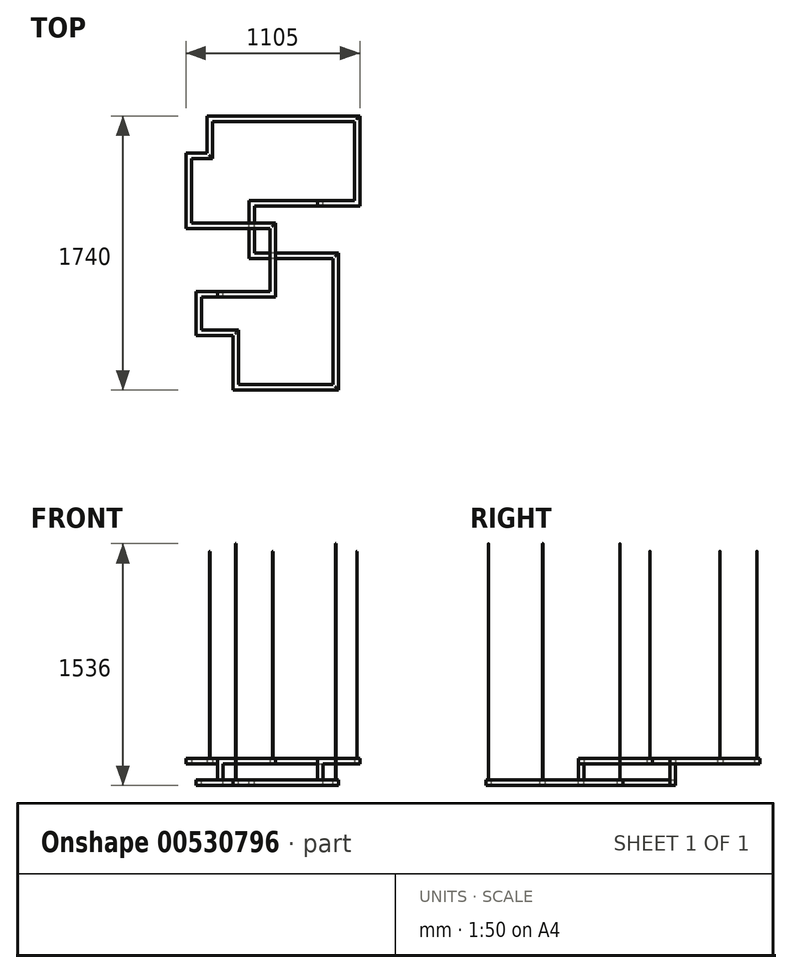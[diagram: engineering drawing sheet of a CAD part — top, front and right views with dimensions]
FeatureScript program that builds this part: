
annotation { "Feature Type Name" : "Feature", "Feature Type Description" : "" }
export const myFeature = defineFeature(function(context is Context, id is Id, definition is map)
    precondition{}
    {
        {
            var Q0;
            Q0=qCreatedBy(makeId("Top.planeOp"),FACE);
            var sketch = newSketch(context, id + "F0", { "sketchPlane" : qUnion([Q0])});
            skLineSegment(sketch, "E0", {"start": v(519.01, 860.28) * mm, "end": v(-510.57, -839.72) * mm, "construction": true});
            skLineSegment(sketch, "E1", {"start": v(-510.57, 860.28) * mm, "end": v(519.01, -839.72) * mm, "construction": true});
            skLineSegment(sketch, "E2", {"start": v(-313.44, -217.5) * mm, "end": v(-17.5, -217.5) * mm, "construction": true});
            skLineSegment(sketch, "E3", {"start": v(-17.5, -217.5) * mm, "end": v(-17.5, 217.5) * mm, "construction": true});
            skLineSegment(sketch, "E4", {"start": v(-17.5, 217.5) * mm, "end": v(-552.5, 217.5) * mm, "construction": true});
            skLineSegment(sketch, "E5", {"start": v(-552.5, 217.5) * mm, "end": v(-552.5, 662.5) * mm, "construction": true});
            skLineSegment(sketch, "E6", {"start": v(-552.5, 662.5) * mm, "end": v(-417.5, 662.5) * mm, "construction": true});
            skLineSegment(sketch, "E7", {"start": v(-417.5, 662.5) * mm, "end": v(-417.5, 897.5) * mm, "construction": true});
            skLineSegment(sketch, "E8", {"start": v(-417.5, 897.5) * mm, "end": v(517.5, 897.5) * mm, "construction": true});
            skLineSegment(sketch, "E9", {"start": v(517.5, 897.5) * mm, "end": v(517.5, 362.5) * mm, "construction": true});
            skLineSegment(sketch, "E10", {"start": v(517.5, 362.5) * mm, "end": v(294.36, 362.5) * mm, "construction": true});
            skLineSegment(sketch, "E11.0", {"start": v(500, 380) * mm, "end": v(265, 380) * mm});
            skLineSegment(sketch, "E11.1", {"start": v(500, 880) * mm, "end": v(500, 380) * mm});
            skLineSegment(sketch, "E11.2", {"start": v(-400, 880) * mm, "end": v(500, 880) * mm});
            skLineSegment(sketch, "E11.3", {"start": v(-400, 645) * mm, "end": v(-400, 880) * mm});
            skLineSegment(sketch, "E11.4", {"start": v(-535, 645) * mm, "end": v(-400, 645) * mm});
            skLineSegment(sketch, "E11.5", {"start": v(-370, -235) * mm, "end": v(0, -235) * mm});
            skLineSegment(sketch, "E11.6", {"start": v(0, -235) * mm, "end": v(0, 235) * mm});
            skLineSegment(sketch, "E11.7", {"start": v(0, 235) * mm, "end": v(-535, 235) * mm});
            skLineSegment(sketch, "E11.8", {"start": v(-535, 235) * mm, "end": v(-535, 645) * mm});
            skLineSegment(sketch, "E12.0", {"start": v(535, 345) * mm, "end": v(265, 345) * mm});
            skLineSegment(sketch, "E12.1", {"start": v(535, 915) * mm, "end": v(535, 345) * mm});
            skLineSegment(sketch, "E12.2", {"start": v(-435, 915) * mm, "end": v(535, 915) * mm});
            skLineSegment(sketch, "E12.3", {"start": v(-435, 680) * mm, "end": v(-435, 915) * mm});
            skLineSegment(sketch, "E12.4", {"start": v(-570, 680) * mm, "end": v(-435, 680) * mm});
            skLineSegment(sketch, "E12.5", {"start": v(-370, -200) * mm, "end": v(-35, -200) * mm});
            skLineSegment(sketch, "E12.6", {"start": v(-35, -200) * mm, "end": v(-35, 200) * mm});
            skLineSegment(sketch, "E12.7", {"start": v(-35, 200) * mm, "end": v(-570, 200) * mm});
            skLineSegment(sketch, "E12.8", {"start": v(-570, 200) * mm, "end": v(-570, 680) * mm});
            skLineSegment(sketch, "E13", {"start": v(265, 380) * mm, "end": v(265, 345) * mm});
            skLineSegment(sketch, "E14", {"start": v(-370, -235) * mm, "end": v(-370, -200) * mm});
            skSolve(sketch);
        }
        {
            var Q0;
            Q0=qSketchRegion(id+"F0",true);
            extrude(context, id + "F1", {"entities" : qUnion([Q0]), "depth" : 35 * mm});
        }
        {
            var Q0;
            Q0=qCreatedBy(makeId("Top.planeOp"),FACE);
            var sketch = newSketch(context, id + "F2", { "sketchPlane" : qUnion([Q0])});
            skLineSegment(sketch, "E15.bottom", {"start": v(-370, -235) * mm, "end": v(-335, -235) * mm});
            skLineSegment(sketch, "E15.top", {"start": v(-370, -200) * mm, "end": v(-335, -200) * mm});
            skLineSegment(sketch, "E15.left", {"start": v(-370, -235) * mm, "end": v(-370, -200) * mm});
            skLineSegment(sketch, "E15.right", {"start": v(-335, -235) * mm, "end": v(-335, -200) * mm});
            skLineSegment(sketch, "E16.bottom", {"start": v(265, 345) * mm, "end": v(300, 345) * mm});
            skLineSegment(sketch, "E16.top", {"start": v(265, 380) * mm, "end": v(300, 380) * mm});
            skLineSegment(sketch, "E16.left", {"start": v(265, 345) * mm, "end": v(265, 380) * mm});
            skLineSegment(sketch, "E16.right", {"start": v(300, 345) * mm, "end": v(300, 380) * mm});
            skSolve(sketch);
        }
        {
            var Q0;
            Q0=qSketchRegion(id+"F2",true);
            extrude(context, id + "F3", {"entities" : qUnion([Q0]), "operationType" : NewBodyOperationType.ADD, "oppositeDirection" : true, "depth" : 100 * mm, "offsetDistance" : 25 * mm});
        }
        {
            var Q0;
            Q0=makeQuery(id+"F3.opExtrude","CAP_FACE",FACE,{"disambiguationData":[OSD([sQuery(id+"F2.wireOp",EDGE,"E15.bottom"),sQuery(id+"F2.wireOp",EDGE,"E15.top"),sQuery(id+"F2.wireOp",EDGE,"E15.left"),sQuery(id+"F2.wireOp",EDGE,"E15.right")])],"isStart":false});
            cPlane(context, id + "F4", {"entities" : qUnion([Q0]), "cplaneType" : CPlaneType.OFFSET, "offset" : 0 * mm, "width" : 150 * mm, "height" : 150 * mm});
        }
        {
            var Q0;
            Q0=qCreatedBy(id+"F4.planeOp",FACE);
            var sketch = newSketch(context, id + "F5", { "sketchPlane" : qUnion([Q0])});
            skLineSegment(sketch, "E17", {"start": v(-352.5, 217.5) * mm, "end": v(-487.5, 217.5) * mm, "construction": true});
            skLineSegment(sketch, "E18", {"start": v(-487.5, 217.5) * mm, "end": v(-487.5, 462.5) * mm, "construction": true});
            skLineSegment(sketch, "E19", {"start": v(-487.5, 462.5) * mm, "end": v(-252.5, 462.5) * mm, "construction": true});
            skLineSegment(sketch, "E20", {"start": v(-252.5, 462.5) * mm, "end": v(-252.5, 807.5) * mm, "construction": true});
            skLineSegment(sketch, "E21", {"start": v(-252.5, 807.5) * mm, "end": v(382.5, 807.5) * mm, "construction": true});
            skLineSegment(sketch, "E22", {"start": v(382.5, 807.5) * mm, "end": v(382.5, -27.5) * mm, "construction": true});
            skLineSegment(sketch, "E23", {"start": v(382.5, -27.5) * mm, "end": v(-152.5, -27.5) * mm, "construction": true});
            skLineSegment(sketch, "E24", {"start": v(-152.5, -27.5) * mm, "end": v(-152.5, -362.5) * mm, "construction": true});
            skLineSegment(sketch, "E25", {"start": v(-152.5, -362.5) * mm, "end": v(282.5, -362.5) * mm, "construction": true});
            skLineSegment(sketch, "E26.0", {"start": v(-170, -380) * mm, "end": v(300, -380) * mm});
            skLineSegment(sketch, "E26.1", {"start": v(-170, -10) * mm, "end": v(-170, -380) * mm});
            skLineSegment(sketch, "E26.2", {"start": v(365, -10) * mm, "end": v(-170, -10) * mm});
            skLineSegment(sketch, "E26.3", {"start": v(365, 790) * mm, "end": v(365, -10) * mm});
            skLineSegment(sketch, "E26.4", {"start": v(-235, 790) * mm, "end": v(365, 790) * mm});
            skLineSegment(sketch, "E26.5", {"start": v(-335, 235) * mm, "end": v(-470, 235) * mm});
            skLineSegment(sketch, "E26.6", {"start": v(-470, 235) * mm, "end": v(-470, 445) * mm});
            skLineSegment(sketch, "E26.7", {"start": v(-470, 445) * mm, "end": v(-235, 445) * mm});
            skLineSegment(sketch, "E26.8", {"start": v(-235, 445) * mm, "end": v(-235, 790) * mm});
            skLineSegment(sketch, "E27.0", {"start": v(-135, -345) * mm, "end": v(300, -345) * mm});
            skLineSegment(sketch, "E27.1", {"start": v(-135, -45) * mm, "end": v(-135, -345) * mm});
            skLineSegment(sketch, "E27.2", {"start": v(400, -45) * mm, "end": v(-135, -45) * mm});
            skLineSegment(sketch, "E27.3", {"start": v(400, 825) * mm, "end": v(400, -45) * mm});
            skLineSegment(sketch, "E27.4", {"start": v(-270, 825) * mm, "end": v(400, 825) * mm});
            skLineSegment(sketch, "E27.5", {"start": v(-335, 200) * mm, "end": v(-505, 200) * mm});
            skLineSegment(sketch, "E27.6", {"start": v(-505, 200) * mm, "end": v(-505, 480) * mm});
            skLineSegment(sketch, "E27.7", {"start": v(-505, 480) * mm, "end": v(-270, 480) * mm});
            skLineSegment(sketch, "E27.8", {"start": v(-270, 480) * mm, "end": v(-270, 825) * mm});
            skLineSegment(sketch, "E28", {"start": v(300, -380) * mm, "end": v(300, -345) * mm});
            skLineSegment(sketch, "E29", {"start": v(-335, 200) * mm, "end": v(-335, 235) * mm});
            skSolve(sketch);
        }
        {
            var Q0;
            Q0=qSketchRegion(id+"F5",true);
            extrude(context, id + "F6", {"entities" : qUnion([Q0]), "operationType" : NewBodyOperationType.ADD, "depth" : 35 * mm});
        }
        {
            var Q0;
            Q0=makeQuery(id+"F6.opExtrude","CAP_FACE",FACE,{"disambiguationData":[OSD([sQuery(id+"F5.wireOp",EDGE,"E26.0"),sQuery(id+"F5.wireOp",EDGE,"E26.1"),sQuery(id+"F5.wireOp",EDGE,"E26.2"),sQuery(id+"F5.wireOp",EDGE,"E26.3"),sQuery(id+"F5.wireOp",EDGE,"E26.4"),sQuery(id+"F5.wireOp",EDGE,"E26.5"),sQuery(id+"F5.wireOp",EDGE,"E26.6"),sQuery(id+"F5.wireOp",EDGE,"E26.7"),sQuery(id+"F5.wireOp",EDGE,"E26.8"),sQuery(id+"F5.wireOp",EDGE,"E27.0"),sQuery(id+"F5.wireOp",EDGE,"E27.1"),sQuery(id+"F5.wireOp",EDGE,"E27.2"),sQuery(id+"F5.wireOp",EDGE,"E27.3"),sQuery(id+"F5.wireOp",EDGE,"E27.4"),sQuery(id+"F5.wireOp",EDGE,"E27.5"),sQuery(id+"F5.wireOp",EDGE,"E27.6"),sQuery(id+"F5.wireOp",EDGE,"E27.7"),sQuery(id+"F5.wireOp",EDGE,"E27.8"),sQuery(id+"F5.wireOp",EDGE,"E28"),sQuery(id+"F5.wireOp",EDGE,"E29")])],"isStart":false});
            extrude(context, id + "F7", {"entities" : qUnion([Q0]), "depth" : 1 * mm});
        }
        {
            var Q0;
            Q0=makeQuery(id+"F6.boolean.opBoolean","MERGE",FACE,{"derivedFrom":[makeQuery(id+"F3.opExtrude","SWEPT_FACE",FACE,{"disambiguationData":[OSD([sQuery(id+"F2.wireOp",EDGE,"E15.right")])]}),makeQuery(id+"F6.opExtrude","SWEPT_FACE",FACE,{"disambiguationData":[OSD([sQuery(id+"F5.wireOp",EDGE,"E29")])]})]});
            var Q1;
            Q1=makeQuery(id+"F6.boolean.opBoolean","MERGE",FACE,{"derivedFrom":[makeQuery(id+"F3.opExtrude","SWEPT_FACE",FACE,{"disambiguationData":[OSD([sQuery(id+"F2.wireOp",EDGE,"E16.right")])]}),makeQuery(id+"F6.opExtrude","SWEPT_FACE",FACE,{"disambiguationData":[OSD([sQuery(id+"F5.wireOp",EDGE,"E28")])]})]});
            extrude(context, id + "F8", {"entities" : qUnion([Q0, Q1]), "depth" : 1 * mm});
        }
        {
            var Q0;
            Q0=makeQuery(id+"F1.opExtrude","CAP_FACE",FACE,{"disambiguationData":[OSD([sQuery(id+"F0.wireOp",EDGE,"E11.0"),sQuery(id+"F0.wireOp",EDGE,"E11.1"),sQuery(id+"F0.wireOp",EDGE,"E11.2"),sQuery(id+"F0.wireOp",EDGE,"E11.3"),sQuery(id+"F0.wireOp",EDGE,"E11.4"),sQuery(id+"F0.wireOp",EDGE,"E11.5"),sQuery(id+"F0.wireOp",EDGE,"E11.6"),sQuery(id+"F0.wireOp",EDGE,"E11.7"),sQuery(id+"F0.wireOp",EDGE,"E11.8"),sQuery(id+"F0.wireOp",EDGE,"E12.0"),sQuery(id+"F0.wireOp",EDGE,"E12.1"),sQuery(id+"F0.wireOp",EDGE,"E12.2"),sQuery(id+"F0.wireOp",EDGE,"E12.3"),sQuery(id+"F0.wireOp",EDGE,"E12.4"),sQuery(id+"F0.wireOp",EDGE,"E12.5"),sQuery(id+"F0.wireOp",EDGE,"E12.6"),sQuery(id+"F0.wireOp",EDGE,"E12.7"),sQuery(id+"F0.wireOp",EDGE,"E12.8"),sQuery(id+"F0.wireOp",EDGE,"E13"),sQuery(id+"F0.wireOp",EDGE,"E14")])],"isStart":true});
            extrude(context, id + "F9", {"entities" : qUnion([Q0]), "depth" : 1 * mm});
        }
        {
            var Q0;
            Q0=makeQuery(id+"F6.opExtrude","CAP_FACE",FACE,{"disambiguationData":[OSD([sQuery(id+"F5.wireOp",EDGE,"E26.0"),sQuery(id+"F5.wireOp",EDGE,"E26.1"),sQuery(id+"F5.wireOp",EDGE,"E26.2"),sQuery(id+"F5.wireOp",EDGE,"E26.3"),sQuery(id+"F5.wireOp",EDGE,"E26.4"),sQuery(id+"F5.wireOp",EDGE,"E26.5"),sQuery(id+"F5.wireOp",EDGE,"E26.6"),sQuery(id+"F5.wireOp",EDGE,"E26.7"),sQuery(id+"F5.wireOp",EDGE,"E26.8"),sQuery(id+"F5.wireOp",EDGE,"E27.0"),sQuery(id+"F5.wireOp",EDGE,"E27.1"),sQuery(id+"F5.wireOp",EDGE,"E27.2"),sQuery(id+"F5.wireOp",EDGE,"E27.3"),sQuery(id+"F5.wireOp",EDGE,"E27.4"),sQuery(id+"F5.wireOp",EDGE,"E27.5"),sQuery(id+"F5.wireOp",EDGE,"E27.6"),sQuery(id+"F5.wireOp",EDGE,"E27.7"),sQuery(id+"F5.wireOp",EDGE,"E27.8"),sQuery(id+"F5.wireOp",EDGE,"E28"),sQuery(id+"F5.wireOp",EDGE,"E29")])],"isStart":true});
            var sketch = newSketch(context, id + "F10", { "sketchPlane" : qUnion([Q0])});
            skPoint(sketch, "E30", {"position": v(382.5, 27.5) * mm});
            skPoint(sketch, "E31", {"position": v(-252.5, -462.5) * mm});
            skCircle(sketch, "E32", {"center": v(-252.5, -462.5) * mm, "radius": 1 * mm});
            skCircle(sketch, "E33", {"center": v(382.5, 27.5) * mm, "radius": 1 * mm});
            skPoint(sketch, "E34", {"position": v(382.5, -807.5) * mm});
            skCircle(sketch, "E35", {"center": v(382.5, -807.5) * mm, "radius": 1 * mm});
            skSolve(sketch);
        }
        {
            var Q0;
            Q0=qSketchRegion(id+"F10",true);
            extrude(context, id + "F11", {"entities" : qUnion([Q0]), "depth" : 1500 * mm});
        }
        {
            var Q0;
            Q0=makeQuery(id+"F1.opExtrude","CAP_FACE",FACE,{"disambiguationData":[OSD([sQuery(id+"F0.wireOp",EDGE,"E11.0"),sQuery(id+"F0.wireOp",EDGE,"E11.1"),sQuery(id+"F0.wireOp",EDGE,"E11.2"),sQuery(id+"F0.wireOp",EDGE,"E11.3"),sQuery(id+"F0.wireOp",EDGE,"E11.4"),sQuery(id+"F0.wireOp",EDGE,"E11.5"),sQuery(id+"F0.wireOp",EDGE,"E11.6"),sQuery(id+"F0.wireOp",EDGE,"E11.7"),sQuery(id+"F0.wireOp",EDGE,"E11.8"),sQuery(id+"F0.wireOp",EDGE,"E12.0"),sQuery(id+"F0.wireOp",EDGE,"E12.1"),sQuery(id+"F0.wireOp",EDGE,"E12.2"),sQuery(id+"F0.wireOp",EDGE,"E12.3"),sQuery(id+"F0.wireOp",EDGE,"E12.4"),sQuery(id+"F0.wireOp",EDGE,"E12.5"),sQuery(id+"F0.wireOp",EDGE,"E12.6"),sQuery(id+"F0.wireOp",EDGE,"E12.7"),sQuery(id+"F0.wireOp",EDGE,"E12.8"),sQuery(id+"F0.wireOp",EDGE,"E13"),sQuery(id+"F0.wireOp",EDGE,"E14")])],"isStart":false});
            var sketch = newSketch(context, id + "F12", { "sketchPlane" : qUnion([Q0])});
            skPoint(sketch, "E36", {"position": v(-17.5, 217.5) * mm});
            skPoint(sketch, "E37", {"position": v(-417.5, 662.5) * mm});
            skPoint(sketch, "E38", {"position": v(517.5, 897.5) * mm});
            skCircle(sketch, "E39", {"center": v(-417.5, 662.5) * mm, "radius": 1 * mm});
            skCircle(sketch, "E40", {"center": v(517.5, 897.5) * mm, "radius": 1 * mm});
            skCircle(sketch, "E41", {"center": v(-17.5, 217.5) * mm, "radius": 1 * mm});
            skSolve(sketch);
        }
        {
            var Q0;
            Q0=qSketchRegion(id+"F12",true);
            extrude(context, id + "F13", {"entities" : qUnion([Q0]), "depth" : 1315 * mm});
        }
    });
